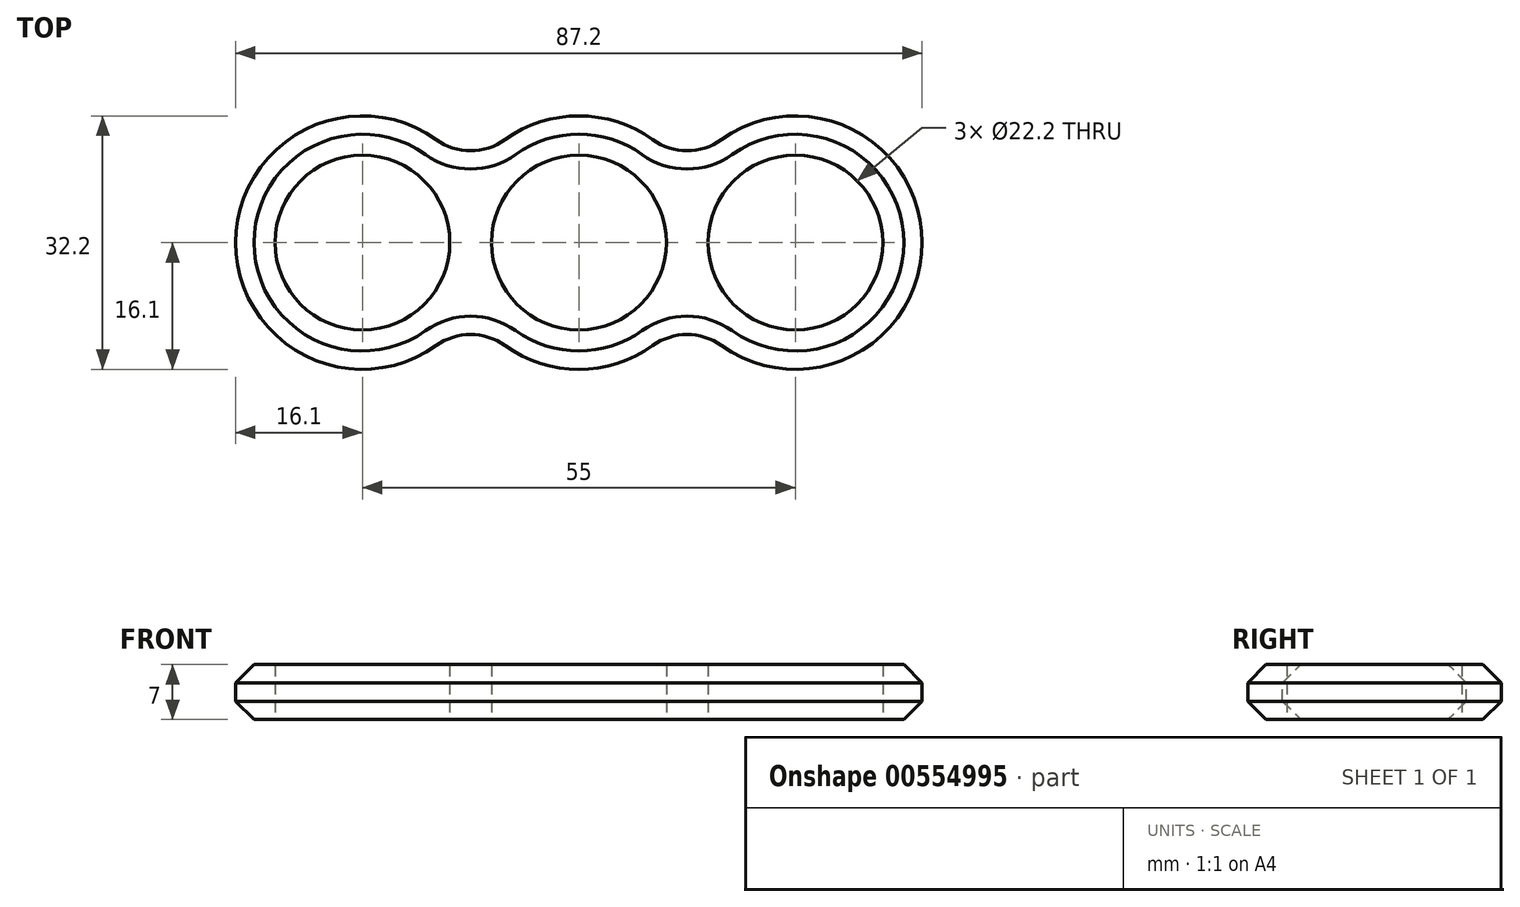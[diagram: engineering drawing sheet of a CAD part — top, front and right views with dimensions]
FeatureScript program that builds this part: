
annotation { "Feature Type Name" : "Feature", "Feature Type Description" : "" }
export const myFeature = defineFeature(function(context is Context, id is Id, definition is map)
    precondition{}
    {
        {
            var Q0;
            Q0=qCreatedBy(makeId("Top.planeOp"),FACE);
            var sketch = newSketch(context, id + "F0", { "sketchPlane" : qUnion([Q0])});
            skCircle(sketch, "E0", {"center": v(0, 0) * mm, "radius": 11.1 * mm});
            skLineSegment(sketch, "E1", {"start": v(0, 0) * mm, "end": v(27.5, 0) * mm, "construction": true});
            skCircle(sketch, "E2", {"center": v(27.5, 0) * mm, "radius": 11.1 * mm});
            skCircle(sketch, "E3", {"center": v(0, 0) * mm, "radius": 16.1 * mm});
            skCircle(sketch, "E4", {"center": v(27.5, 0) * mm, "radius": 16.1 * mm});
            skCircle(sketch, "E5.MirrorC", {"center": v(-27.5, 0) * mm, "radius": 16.1 * mm});
            skCircle(sketch, "E6.MirrorC", {"center": v(-27.5, 0) * mm, "radius": 11.1 * mm});
            skSolve(sketch);
        }
        {
            var Q0;
            Q0 = qSketchRegion(id + "F0", true);
            extrude(context, id + "F1", {"entities" : qUnion([Q0]), "depth" : 7 * mm, "offsetDistance" : 25 * mm});
        }
        {
            var Q0;
            {var subQ0=sQuery(id+"F0.wireOp",EDGE,"E5.MirrorC");var subQ1=sQuery(id+"F0.wireOp",EDGE,"E3");Q0=makeQuery(id+"F1.opExtrude","SWEPT_EDGE",EDGE,{"disambiguationData":[OSD([subQ1,subQ0]),TDD([makeQuery(id+"F0.imprint","INTERSECT",VERTEX,{"disambiguationData":[OD(0.0)],"derivedFrom":[subQ1,subQ0]})])]});}
            var Q1;
            {var subQ0=sQuery(id+"F0.wireOp",EDGE,"E4");var subQ1=sQuery(id+"F0.wireOp",EDGE,"E3");Q1=makeQuery(id+"F1.opExtrude","SWEPT_EDGE",EDGE,{"disambiguationData":[OSD([subQ1,subQ0]),TDD([makeQuery(id+"F0.imprint","INTERSECT",VERTEX,{"disambiguationData":[OD(0.0)],"derivedFrom":[subQ1,subQ0]})])]});}
            var Q2;
            {var subQ0=sQuery(id+"F0.wireOp",EDGE,"E5.MirrorC");var subQ1=sQuery(id+"F0.wireOp",EDGE,"E3");Q2=makeQuery(id+"F1.opExtrude","SWEPT_EDGE",EDGE,{"disambiguationData":[OSD([subQ1,subQ0]),TDD([makeQuery(id+"F0.imprint","INTERSECT",VERTEX,{"disambiguationData":[OD(1.0)],"derivedFrom":[subQ1,subQ0]})])]});}
            var Q3;
            {var subQ0=sQuery(id+"F0.wireOp",EDGE,"E4");var subQ1=sQuery(id+"F0.wireOp",EDGE,"E3");Q3=makeQuery(id+"F1.opExtrude","SWEPT_EDGE",EDGE,{"disambiguationData":[OSD([subQ1,subQ0]),TDD([makeQuery(id+"F0.imprint","INTERSECT",VERTEX,{"disambiguationData":[OD(1.0)],"derivedFrom":[subQ1,subQ0]})])]});}
            fillet(context, id + "F2", {"entities" : qUnion([Q0, Q1, Q2, Q3]), "radius" : 7.5 * mm, "tangentPropagation" : true, "allowEdgeOverflow" : false});
        }
        {
            var Q0;
            {var subQ0=sQuery(id+"F0.wireOp",EDGE,"E3");Q0=makeQuery(id+"F1.opExtrude","CAP_EDGE",EDGE,{"disambiguationData":[OSD([subQ0]),TDD([makeQuery(id+"F0.imprint","IMPRINT",EDGE,{"disambiguationData":[TD([[makeQuery(id+"F0.imprint","INTERSECT",VERTEX,{"disambiguationData":[OD(0.0)],"derivedFrom":[subQ0,sQuery(id+"F0.wireOp",EDGE,"E5.MirrorC")]}),1.0]])],"derivedFrom":subQ0})])],"isStart":false});}
            var Q1;
            {var subQ0=sQuery(id+"F0.wireOp",EDGE,"E5.MirrorC");var subQ1=sQuery(id+"F0.wireOp",EDGE,"E3");Q1=makeQuery(id+"F2.opFillet","BLEND_EDGE",EDGE,{"blendedFrom":[makeQuery(id+"F1.opExtrude","SWEPT_EDGE",EDGE,{"disambiguationData":[OSD([subQ1,subQ0]),TDD([makeQuery(id+"F0.imprint","INTERSECT",VERTEX,{"disambiguationData":[OD(0.0)],"derivedFrom":[subQ1,subQ0]})])]}),makeQuery(id+"F1.opExtrude","CAP_FACE",FACE,{"disambiguationData":[OSD([sQuery(id+"F0.wireOp",EDGE,"E0"),sQuery(id+"F0.wireOp",EDGE,"E2"),subQ1,sQuery(id+"F0.wireOp",EDGE,"E4"),subQ0,sQuery(id+"F0.wireOp",EDGE,"E6.MirrorC")])],"isStart":false})],"blendedInto":[makeQuery(id+"F1.opExtrude","CAP_FACE",FACE,{"disambiguationData":[OSD([sQuery(id+"F0.wireOp",EDGE,"E0"),sQuery(id+"F0.wireOp",EDGE,"E2"),subQ1,sQuery(id+"F0.wireOp",EDGE,"E4"),subQ0,sQuery(id+"F0.wireOp",EDGE,"E6.MirrorC")])],"isStart":false})]});}
            var Q2;
            Q2=makeQuery(id+"F1.opExtrude","CAP_EDGE",EDGE,{"disambiguationData":[OSD([sQuery(id+"F0.wireOp",EDGE,"E5.MirrorC")])],"isStart":true});
            chamfer(context, id + "F3", {"entities" : qUnion([Q0, Q1, Q2]), "width" : 2.33 * mm, "tangentPropagation" : true});
        }
    });
